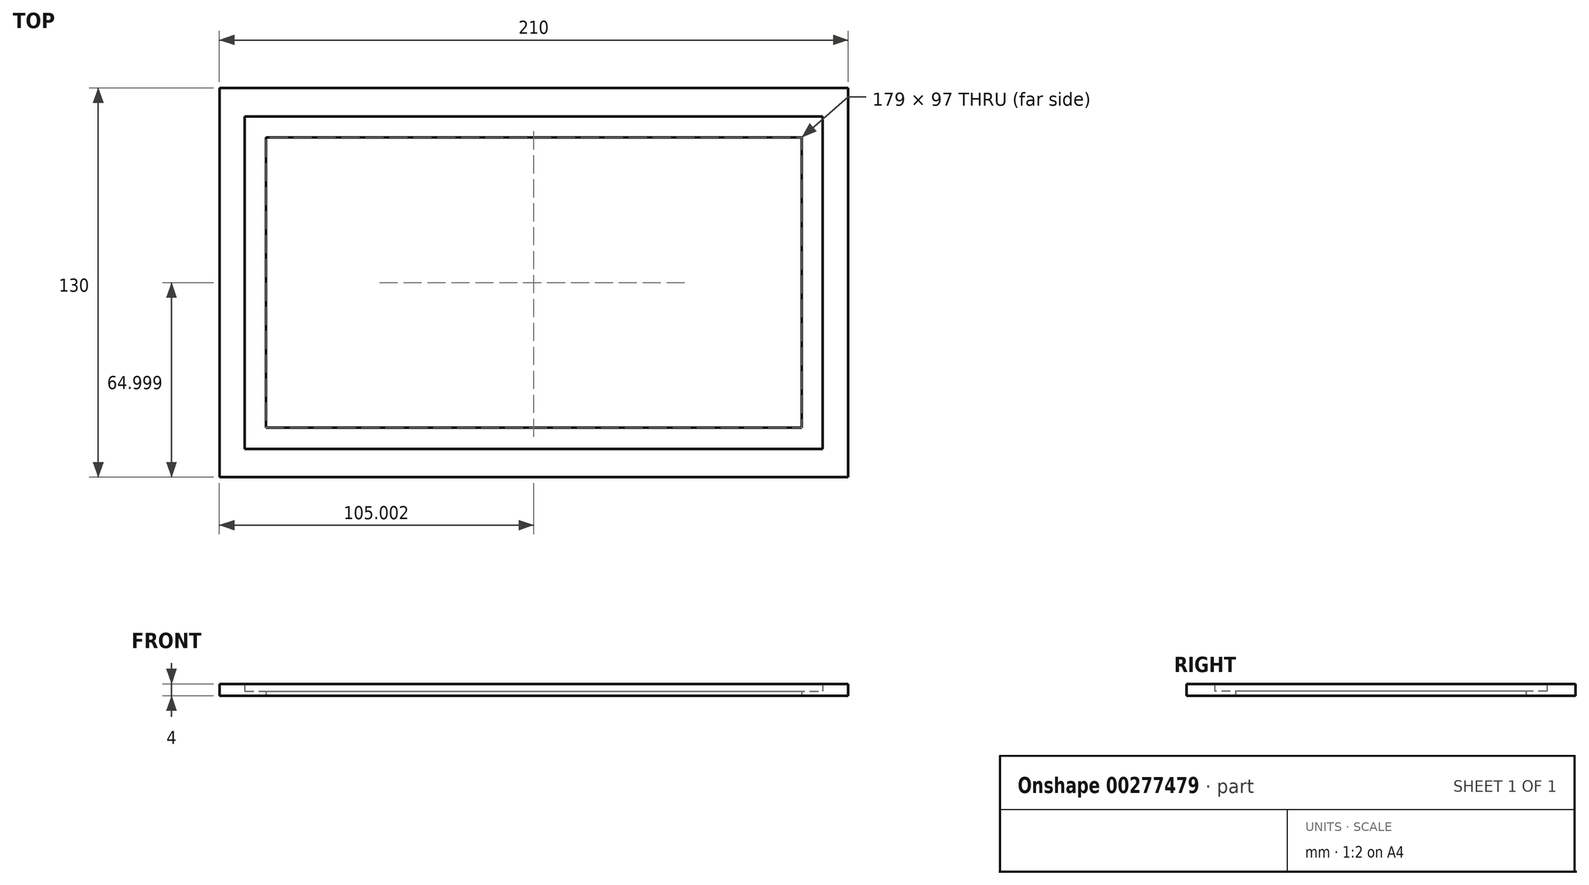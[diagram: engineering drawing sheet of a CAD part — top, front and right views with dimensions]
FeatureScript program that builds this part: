
annotation { "Feature Type Name" : "Feature", "Feature Type Description" : "" }
export const myFeature = defineFeature(function(context is Context, id is Id, definition is map)
    precondition{}
    {
        {
            var Q0;
            Q0=qCreatedBy(makeId("Top.planeOp"),FACE);
            var sketch = newSketch(context, id + "F0", { "sketchPlane" : qUnion([Q0])});
            skLineSegment(sketch, "E0.bottom", {"start": v(-56.79, 79.24) * mm, "end": v(153.21, 79.24) * mm});
            skLineSegment(sketch, "E0.top", {"start": v(-56.79, -50.76) * mm, "end": v(153.21, -50.76) * mm});
            skLineSegment(sketch, "E0.left", {"start": v(-56.79, 79.24) * mm, "end": v(-56.79, -50.76) * mm});
            skLineSegment(sketch, "E0.right", {"start": v(153.21, 79.24) * mm, "end": v(153.21, -50.76) * mm});
            skLineSegment(sketch, "E1.bottom", {"start": v(-48.29, 69.74) * mm, "end": v(144.71, 69.74) * mm});
            skLineSegment(sketch, "E1.top", {"start": v(-48.29, -41.26) * mm, "end": v(144.71, -41.26) * mm});
            skLineSegment(sketch, "E1.left", {"start": v(-48.29, 69.74) * mm, "end": v(-48.29, -41.26) * mm});
            skLineSegment(sketch, "E1.right", {"start": v(144.71, 69.74) * mm, "end": v(144.71, -41.26) * mm});
            skLineSegment(sketch, "E2.bottom", {"start": v(-41.29, 62.74) * mm, "end": v(137.71, 62.74) * mm});
            skLineSegment(sketch, "E2.top", {"start": v(-41.29, -34.26) * mm, "end": v(137.71, -34.26) * mm});
            skLineSegment(sketch, "E2.left", {"start": v(-41.29, 62.74) * mm, "end": v(-41.29, -34.26) * mm});
            skLineSegment(sketch, "E2.right", {"start": v(137.71, 62.74) * mm, "end": v(137.71, -34.26) * mm});
            skSolve(sketch);
        }
        {
            var Q0;
            Q0=makeQuery(id+"F0.imprint","IMPRINT",FACE,{"disambiguationData":[TD([[makeQuery(id+"F0.imprint","IMPRINT",EDGE,{"derivedFrom":sQuery(id+"F0.wireOp",EDGE,"E0.bottom")}),-1.0]])]});
            extrude(context, id + "F1", {"entities" : qUnion([Q0]), "depth" : 4 * mm});
        }
        {
            var Q0;
            Q0=makeQuery(id+"F0.imprint","IMPRINT",FACE,{"disambiguationData":[TD([[makeQuery(id+"F0.imprint","IMPRINT",EDGE,{"derivedFrom":sQuery(id+"F0.wireOp",EDGE,"E1.bottom")}),-1.0]])]});
            extrude(context, id + "F2", {"entities" : qUnion([Q0]), "operationType" : NewBodyOperationType.ADD, "depth" : 1.5 * mm});
        }
    });
